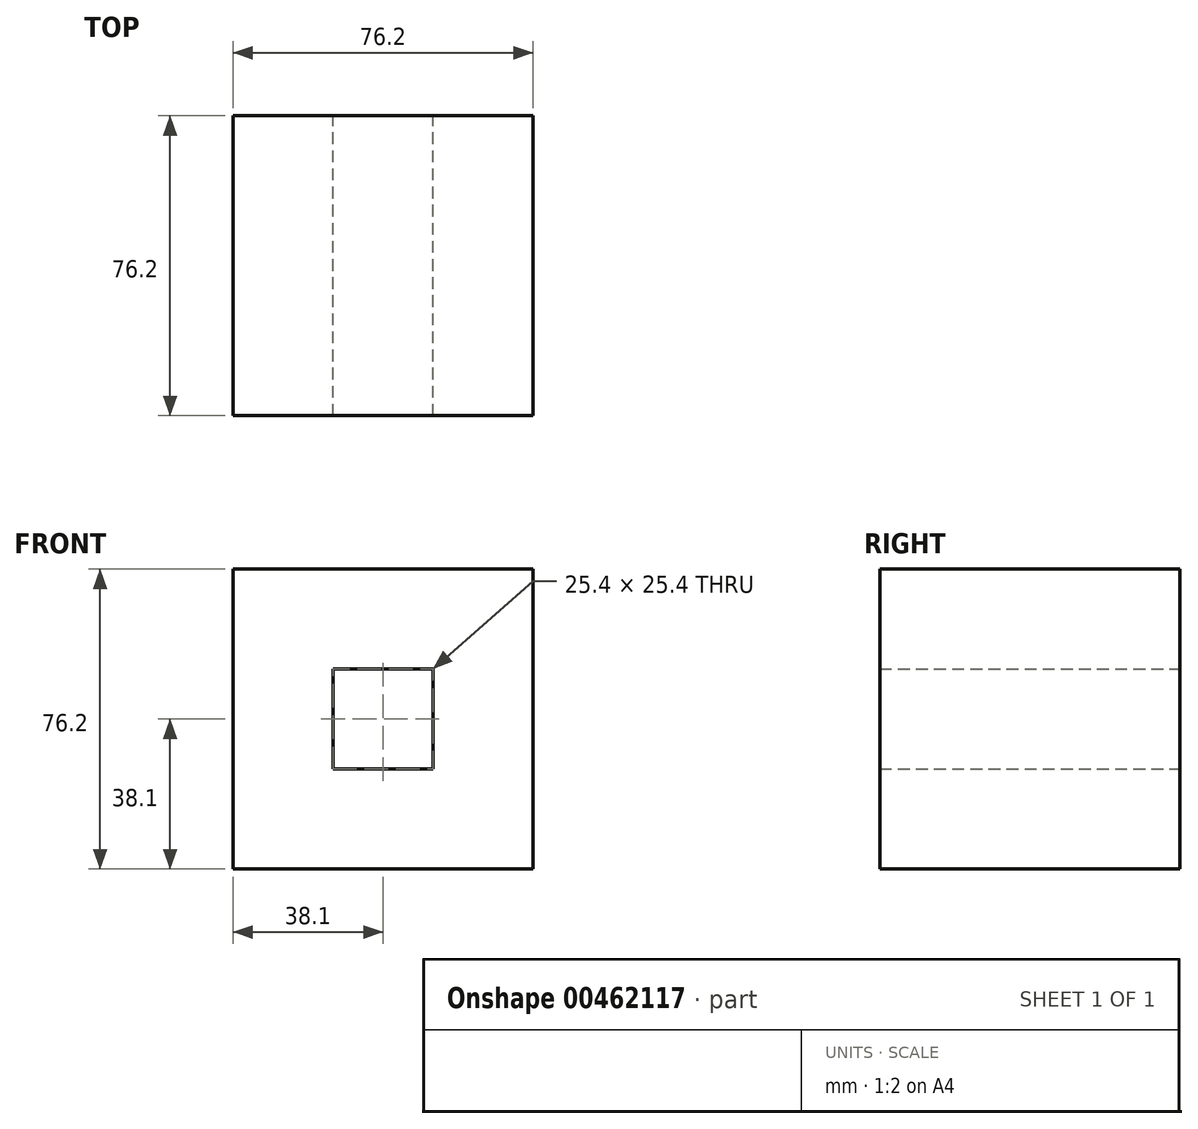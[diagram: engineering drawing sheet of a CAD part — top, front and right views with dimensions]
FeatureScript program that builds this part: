
annotation { "Feature Type Name" : "Feature", "Feature Type Description" : "" }
export const myFeature = defineFeature(function(context is Context, id is Id, definition is map)
    precondition{}
    {
        {
            var Q0;
            Q0=qCreatedBy(makeId("Front.planeOp"),FACE);
            var sketch = newSketch(context, id + "F0", { "sketchPlane" : qUnion([Q0])});
            skLineSegment(sketch, "E0.bottom", {"start": v(-38.1, 38.1) * mm, "end": v(38.1, 38.1) * mm});
            skLineSegment(sketch, "E0.top", {"start": v(-38.1, -38.1) * mm, "end": v(38.1, -38.1) * mm});
            skLineSegment(sketch, "E0.left", {"start": v(-38.1, 38.1) * mm, "end": v(-38.1, -38.1) * mm});
            skLineSegment(sketch, "E0.right", {"start": v(38.1, 38.1) * mm, "end": v(38.1, -38.1) * mm});
            skPoint(sketch, "E0.middle", {"position": v(0, 0) * mm});
            skLineSegment(sketch, "E1.bottom", {"start": v(-12.7, 12.7) * mm, "end": v(12.7, 12.7) * mm});
            skLineSegment(sketch, "E1.top", {"start": v(-12.7, -12.7) * mm, "end": v(12.7, -12.7) * mm});
            skLineSegment(sketch, "E1.left", {"start": v(-12.7, 12.7) * mm, "end": v(-12.7, -12.7) * mm});
            skLineSegment(sketch, "E1.right", {"start": v(12.7, 12.7) * mm, "end": v(12.7, -12.7) * mm});
            skSolve(sketch);
        }
        {
            var Q0;
            Q0=makeQuery(id+"F0.imprint","IMPRINT",FACE,{"disambiguationData":[TD([[makeQuery(id+"F0.imprint","IMPRINT",EDGE,{"derivedFrom":sQuery(id+"F0.wireOp",EDGE,"E0.bottom")}),-1.0]])]});
            extrude(context, id + "F1", {"entities" : qUnion([Q0]), "depth" : 76.2 * mm});
        }
    });
